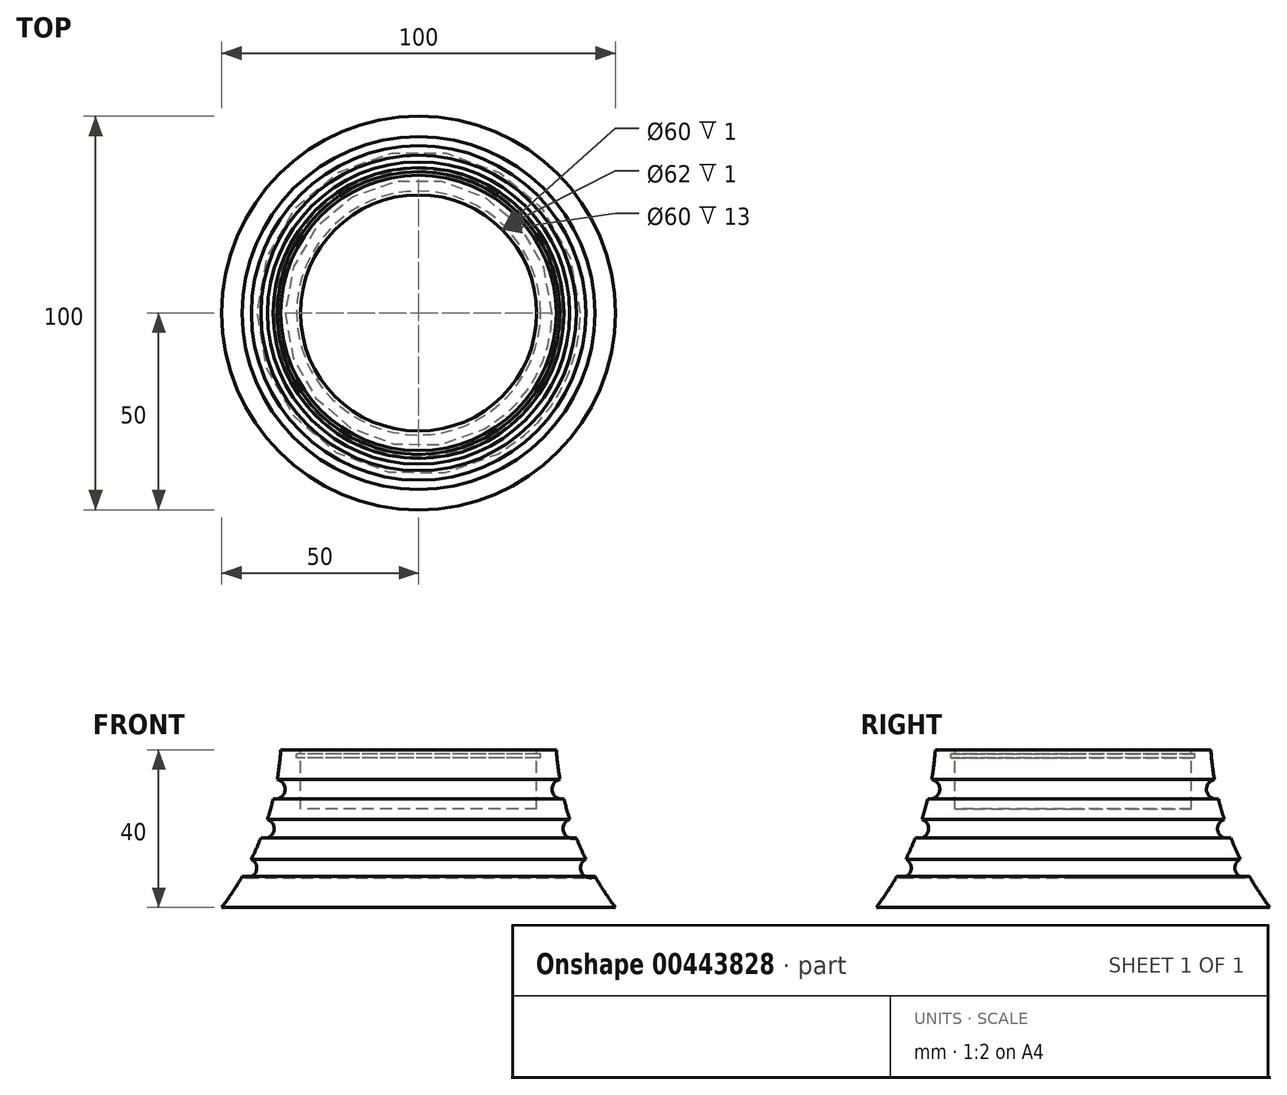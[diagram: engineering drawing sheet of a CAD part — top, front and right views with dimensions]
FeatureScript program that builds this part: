
annotation { "Feature Type Name" : "Feature", "Feature Type Description" : "" }
export const myFeature = defineFeature(function(context is Context, id is Id, definition is map)
    precondition{}
    {
        {
            var Q0;
            Q0=qCreatedBy(makeId("Front.planeOp"),FACE);
            var sketch = newSketch(context, id + "F0", { "sketchPlane" : qUnion([Q0])});
            skLineSegment(sketch, "E0", {"start": v(0, 0) * mm, "end": v(-30, 0) * mm});
            skLineSegment(sketch, "E1", {"start": v(-30, 0) * mm, "end": v(-30, -25) * mm});
            skLineSegment(sketch, "E2", {"start": v(-30, -25) * mm, "end": v(20, -25) * mm});
            skLineSegment(sketch, "E3", {"start": v(0, 0) * mm, "end": v(0, 13) * mm});
            skLineSegment(sketch, "E4", {"start": v(0, 13) * mm, "end": v(1, 13) * mm});
            skLineSegment(sketch, "E5", {"start": v(1, 13) * mm, "end": v(1, 14) * mm});
            skLineSegment(sketch, "E6", {"start": v(1, 14) * mm, "end": v(0, 14) * mm});
            skLineSegment(sketch, "E7", {"start": v(0, 14) * mm, "end": v(0, 15) * mm});
            skLineSegment(sketch, "E8", {"start": v(0, 15) * mm, "end": v(5, 15) * mm});
            skArc(sketch, "E9", {"start": v(5, 15) * mm, "mid": v(5.36, 11.22) * mm, "end": v(5.91, 7.46) * mm});
            skArc(sketch, "E10", {"start": v(8.4, -2.63) * mm, "mid": v(6.84, -5.84) * mm, "end": v(10.07, -7.34) * mm});
            skArc(sketch, "E11", {"start": v(5.91, 7.46) * mm, "mid": v(3.93, 4.5) * mm, "end": v(6.93, 2.56) * mm});
            skArc(sketch, "E12", {"start": v(12.48, -12.77) * mm, "mid": v(11.4, -16.17) * mm, "end": v(14.82, -17.19) * mm});
            skArc(sketch, "E13.trimOffspring", {"start": v(14.82, -17.19) * mm, "mid": v(17.3, -21.17) * mm, "end": v(20, -25) * mm});
            skArc(sketch, "E14.trimOffspring", {"start": v(10.07, -7.34) * mm, "mid": v(11.22, -10.08) * mm, "end": v(12.48, -12.77) * mm});
            skArc(sketch, "E15.trimOffspring", {"start": v(6.93, 2.56) * mm, "mid": v(7.61, -0.05) * mm, "end": v(8.4, -2.63) * mm});
            skSolve(sketch);
        }
        {
            var Q0;
            Q0=makeQuery(id+"F0.imprint","IMPRINT",FACE,{"disambiguationData":[TD([[makeQuery(id+"F0.imprint","IMPRINT",EDGE,{"derivedFrom":sQuery(id+"F0.wireOp",EDGE,"E0")}),1.0]])]});
            var Q1;
            Q1=sQuery(id+"F0.wireOp",EDGE,"E1");
            revolve(context, id + "F1", {"entities" : qUnion([Q0]), "axis" : qUnion([Q1]), "revolveType" : RevolveType.FULL});
        }
    });
